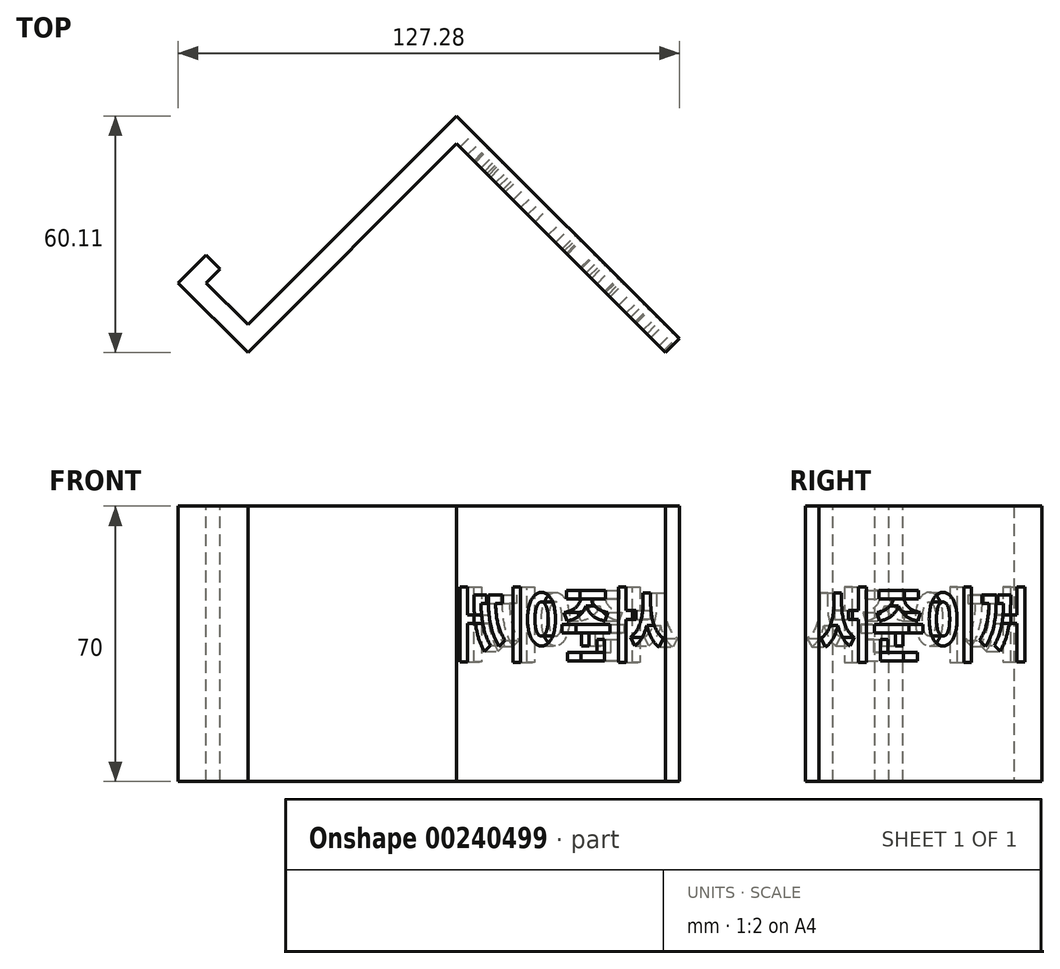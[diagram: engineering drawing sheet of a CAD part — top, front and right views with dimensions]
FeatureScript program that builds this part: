
annotation { "Feature Type Name" : "Feature", "Feature Type Description" : "" }
export const myFeature = defineFeature(function(context is Context, id is Id, definition is map)
    precondition{}
    {
        {
            var Q0;
            Q0=qCreatedBy(makeId("Top.planeOp"),FACE);
            var sketch = newSketch(context, id + "F0", { "sketchPlane" : qUnion([Q0])});
            skLineSegment(sketch, "E0", {"start": v(-11.75, -41.76) * mm, "end": v(25.55, -41.76) * mm, "construction": true});
            skLineSegment(sketch, "E1", {"start": v(-18, -33.6) * mm, "end": v(38.57, 22.97) * mm});
            skLineSegment(sketch, "E2", {"start": v(38.57, 22.97) * mm, "end": v(95.14, -33.6) * mm});
            skLineSegment(sketch, "E3.0", {"start": v(38.57, 15.9) * mm, "end": v(91.6, -37.14) * mm});
            skLineSegment(sketch, "E3.1", {"start": v(-14.46, -37.14) * mm, "end": v(38.57, 15.9) * mm});
            skLineSegment(sketch, "E4", {"start": v(-18, -33.6) * mm, "end": v(-14.46, -37.14) * mm});
            skLineSegment(sketch, "E5", {"start": v(95.14, -33.6) * mm, "end": v(91.6, -37.14) * mm});
            skSolve(sketch);
        }
        {
            var Q0;
            Q0 = qSketchRegion(id + "F0", true);
            extrude(context, id + "F1", {"entities" : qUnion([Q0]), "depth" : 70 * mm});
        }
        {
            var Q0;
            Q0=makeQuery(id+"F1.opExtrude","SWEPT_FACE",FACE,{"disambiguationData":[OSD([sQuery(id+"F0.wireOp",EDGE,"E1")])]});
            var sketch = newSketch(context, id + "F2", { "sketchPlane" : qUnion([Q0])});
            skLineSegment(sketch, "E6.bottom", {"start": v(31.48, 0) * mm, "end": v(36.48, 0) * mm});
            skLineSegment(sketch, "E6.top", {"start": v(31.48, 70) * mm, "end": v(36.48, 70) * mm});
            skLineSegment(sketch, "E6.left", {"start": v(31.48, 0) * mm, "end": v(31.48, 70) * mm});
            skLineSegment(sketch, "E6.right", {"start": v(36.48, 0) * mm, "end": v(36.48, 70) * mm});
            skSolve(sketch);
        }
        {
            var Q0;
            Q0 = qSketchRegion(id + "F2", true);
            extrude(context, id + "F3", {"entities" : qUnion([Q0]), "operationType" : NewBodyOperationType.ADD, "depth" : 20 * mm});
        }
        {
            var Q0;
            Q0=makeQuery(id+"F3.opExtrude","SWEPT_FACE",FACE,{"disambiguationData":[OSD([sQuery(id+"F2.wireOp",EDGE,"E6.left")])]});
            var sketch = newSketch(context, id + "F4", { "sketchPlane" : qUnion([Q0])});
            skLineSegment(sketch, "E7.bottom", {"start": v(3.96, 0) * mm, "end": v(8.96, 0) * mm});
            skLineSegment(sketch, "E7.top", {"start": v(3.96, 70) * mm, "end": v(8.96, 70) * mm});
            skLineSegment(sketch, "E7.left", {"start": v(3.96, 0) * mm, "end": v(3.96, 70) * mm});
            skLineSegment(sketch, "E7.right", {"start": v(8.96, 0) * mm, "end": v(8.96, 70) * mm});
            skSolve(sketch);
        }
        {
            var Q0;
            Q0 = qSketchRegion(id + "F4", true);
            extrude(context, id + "F5", {"entities" : qUnion([Q0]), "operationType" : NewBodyOperationType.ADD, "depth" : 5 * mm});
        }
        {
            var Q0;
            Q0=makeQuery(id+"F1.opExtrude","SWEPT_FACE",FACE,{"disambiguationData":[OSD([sQuery(id+"F0.wireOp",EDGE,"E2")])]});
            var sketch = newSketch(context, id + "F6", { "sketchPlane" : qUnion([Q0])});
            skText(sketch, "E8", { "text": "서준이꺼", "fontName": "NotoSansCJKkr-Bold.otf"});
            const initialGuessF6  = {"E8": [-0.09104, 0.03212, 1, 0, 0.0149]};
            skSetInitialGuess(sketch, initialGuessF6);
            skSolve(sketch);
        }
        {
            var Q0;
            Q0 = qSketchRegion(id + "F6", true);
            extrude(context, id + "F7", {"entities" : qUnion([Q0]), "operationType" : NewBodyOperationType.REMOVE, "oppositeDirection" : true, "depth" : 23.9 * mm});
        }
    });
